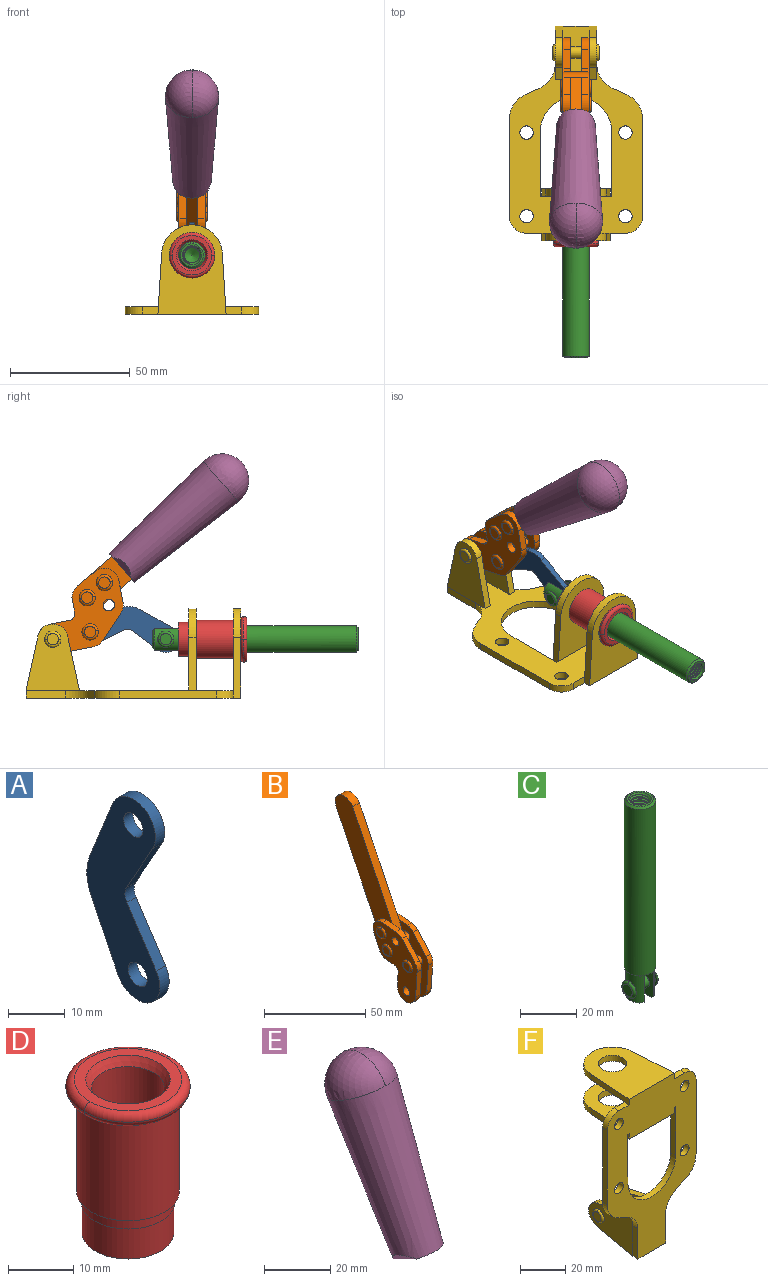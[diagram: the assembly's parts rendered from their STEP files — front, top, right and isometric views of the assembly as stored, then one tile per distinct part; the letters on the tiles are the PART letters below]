
ASSEMBLY  parts=6 mates=6
PART A: 12 faces, bbox 2.3x18.2x42.8 mm
  f0: cylinder r=2.4mm len=4.8mm, axis (1,0,0), area 34.9mm2, adj f4,f11
  f1: cylinder r=10.41mm len=8.47mm, axis (1,0,0), area 20.2mm2, adj f4,f9,f10,f11
  f2: cylinder r=3.05mm len=3.16mm, axis (1,0,0), area 7.7mm2, adj f4,f6,f7,f11
  f3: cylinder r=2.4mm len=4.8mm, axis (1,0,0), area 34.9mm2, adj f4,f11
  f4: plane 42.81x18.23mm, normal (-1,0,0), area 414.1mm2, adj f0,f1,f2,f3,f5,f6,f7,f8
  f5: cylinder r=5.54mm len=10.67mm, axis (1,0,0), area 41.8mm2, adj f4,f6,f10,f11
  f6: plane 11.66x6.53mm, normal (0,-0.87,-0.49), area 30.9mm2, adj f2,f4,f5,f11
  f7: plane 11.17x7.33mm, normal (0,-0.84,0.55), area 30.9mm2, adj f2,f4,f8,f11
  f8: cylinder r=5.54mm len=10.51mm, axis (1,0,0), area 41.8mm2, adj f4,f7,f9,f11
  f9: plane 13.67x6.67mm, normal (0,0.9,-0.44), area 35.1mm2, adj f1,f4,f8,f11
  f10: plane 14.1x5.7mm, normal (0,0.93,0.37), area 35.1mm2, adj f1,f4,f5,f11
  f11: plane 42.81x18.23mm, normal (1,0,0), area 414.1mm2, adj f0,f1,f2,f3,f5,f6,f7,f8
PART B: 59 faces, bbox 12.9x60.2x99.6 mm
  f0: torus R=2.39mm, axis (-1,0,0), area 14.9mm2, adj f20,f43,f51
  f1: torus R=2.39mm, axis (-1,0,0), area 14.9mm2, adj f19,f42,f51
  f2: torus R=2.39mm, axis (-1,0,0), area 14.9mm2, adj f18,f35,f51
  f3: torus R=2.39mm, axis (-1,0,0), area 14.9mm2, adj f14,f17,f23
  f4: torus R=2.39mm, axis (-1,0,0), area 14.9mm2, adj f13,f16,f23
  f5: torus R=2.39mm, axis (-1,0,0), area 14.9mm2, adj f12,f15,f23
  f6: cylinder r=2.39mm len=4.78mm, axis (1,0,0), area 46.5mm2, adj f48,f50,f51
  f7: cylinder r=2.39mm len=4.78mm, axis (1,0,0), area 46.5mm2, adj f50,f51
  f8: cylinder r=6.35mm len=12.68mm, axis (1,0,0), area 61.8mm2, adj f38,f39,f50,f51
  f9: cylinder r=2.39mm len=4.78mm, axis (-1,0,0), area 70.5mm2, adj f46,f50
  f10: cylinder r=2.39mm len=4.78mm, axis (-1,0,0), area 46.5mm2, adj f23,f45,f46
  f11: cylinder r=2.39mm len=4.78mm, axis (-1,0,0), area 46.5mm2, adj f23,f46
  f12: plane 4.78x4.78mm, normal (1,0,0), area 17.9mm2, adj f5,f15
  f13: plane 4.78x4.78mm, normal (1,0,0), area 17.9mm2, adj f4,f16
  f14: plane 4.78x4.78mm, normal (1,0,0), area 17.9mm2, adj f3,f17
  f15: torus R=2.39mm, axis (-1,0,0), area 14.9mm2, adj f5,f12,f23
  f16: torus R=2.39mm, axis (-1,0,0), area 14.9mm2, adj f4,f13,f23
  f17: torus R=2.39mm, axis (-1,0,0), area 14.9mm2, adj f3,f14,f23
  f18: plane 4.78x4.78mm, normal (-1,0,0), area 17.9mm2, adj f2,f35
  f19: plane 4.78x4.78mm, normal (-1,0,0), area 17.9mm2, adj f1,f42
  f20: plane 4.78x4.78mm, normal (-1,0,0), area 17.9mm2, adj f0,f43
  f21: plane 2.26x0.2mm, normal (1,0,0), area 0.2mm2, adj f31,f44
  f22: plane 2.26x0.2mm, normal (-1,0,0), area 0.2mm2, adj f41,f44
  f23: plane 39.37x30.77mm, normal (1,0,0), area 565.5mm2, adj f3,f4,f5,f10,f11,f15,f16,f17
  f24: cylinder r=6.1mm len=4.15mm, axis (-1,0,0), area 14.7mm2, adj f23,f25,f32,f46
  f25: plane 10.25x9.01mm, normal (0,-0.75,0.66), area 42.3mm2, adj f23,f24,f26,f46
  f26: cylinder r=6.35mm len=4.64mm, axis (-1,0,0), area 15.6mm2, adj f23,f25,f27,f46
  f27: plane 15.84x3.1mm, normal (0,-1,-0.07), area 49.2mm2, adj f23,f26,f28,f46
  f28: cylinder r=6.35mm len=12.68mm, axis (-1,0,0), area 61.8mm2, adj f23,f27,f29,f46
  f29: plane 8.11x3.1mm, normal (0,1,0.07), area 25.2mm2, adj f23,f28,f30,f46
  f30: cylinder r=3.05mm len=3.25mm, axis (-1,0,0), area 14.8mm2, adj f23,f29,f31,f46
  f31: plane 5.99x3.1mm, normal (0,0.07,-1), area 18.6mm2, adj f21,f23,f30,f44,f46
  f32: plane 9.5x3.1mm, normal (0,-0.07,1), area 29.5mm2, adj f23,f24,f33,f46,f47
  f33: cylinder r=6.1mm len=8.63mm, axis (-1,0,0), area 39.1mm2, adj f23,f32,f34,f47
  f34: plane 8.65x3.96mm, normal (0,0.91,-0.42), area 29.5mm2, adj f23,f33,f44,f47
  f35: torus R=2.39mm, axis (-1,0,0), area 14.9mm2, adj f2,f18,f51
  f36: plane 10.25x9.01mm, normal (0,-0.75,0.66), area 42.3mm2, adj f37,f49,f50,f51
  f37: cylinder r=6.35mm len=4.64mm, axis (1,0,0), area 15.6mm2, adj f36,f38,f50,f51
  f38: plane 15.84x3.1mm, normal (0,-1,-0.07), area 49.2mm2, adj f8,f37,f50,f51
  f39: plane 8.11x3.1mm, normal (0,1,0.07), area 25.2mm2, adj f8,f40,f50,f51
  f40: cylinder r=3.05mm len=3.25mm, axis (1,0,0), area 14.8mm2, adj f39,f41,f50,f51
  f41: plane 5.99x3.1mm, normal (0,0.07,-1), area 18.6mm2, adj f22,f40,f44,f50,f51
  f42: torus R=2.39mm, axis (-1,0,0), area 14.9mm2, adj f1,f19,f51
  f43: torus R=2.39mm, axis (-1,0,0), area 14.9mm2, adj f0,f20,f51
  f44: cylinder r=6.35mm len=12.12mm, axis (-1,0,0), area 128.9mm2, adj f21,f22,f23,f31,f34,f41,f46,f47
  f45: plane 2.65x1.35mm, normal (1,0,0), area 1mm2, adj f10,f55
  f46: plane 39.08x20.42mm, normal (-1,0,0), area 412.5mm2, adj f9,f10,f11,f24,f25,f26,f27,f28
  f47: plane 77.62x39.82mm, normal (1,0,0), area 850mm2, adj f32,f33,f34,f44,f53,f54,f55
  f48: plane 2.65x1.35mm, normal (-1,0,0), area 1mm2, adj f6,f55
  f49: cylinder r=6.1mm len=4.15mm, axis (1,0,0), area 14.7mm2, adj f36,f50,f51,f56
  f50: plane 39.08x20.42mm, normal (1,0,0), area 412.5mm2, adj f6,f7,f8,f9,f36,f37,f38,f39
  f51: plane 39.37x30.77mm, normal (-1,0,0), area 565.5mm2, adj f0,f1,f2,f6,f7,f8,f35,f36
  f52: plane 8.65x3.96mm, normal (0,0.91,-0.42), area 29.5mm2, adj f44,f51,f57,f58
  f53: plane 68.49x33.4mm, normal (0,0.9,-0.44), area 358.1mm2, adj f44,f47,f54,f58
  f54: cylinder r=6.35mm len=12.06mm, axis (1,0,0), area 93.7mm2, adj f47,f53,f55,f58
  f55: plane 68.49x33.4mm, normal (0,-0.9,0.44), area 358.1mm2, adj f44,f45,f46,f47,f48,f50,f54,f58
  f56: plane 9.5x3.1mm, normal (0,-0.07,1), area 29.5mm2, adj f49,f50,f51,f57,f58
  f57: cylinder r=6.1mm len=8.63mm, axis (1,0,0), area 39.1mm2, adj f51,f52,f56,f58
  f58: plane 77.62x39.82mm, normal (-1,0,0), area 850mm2, adj f44,f52,f53,f54,f55,f56,f57
PART C: 48 faces, bbox 12.6x11.1x86.1 mm
  f0: torus R=2.41mm, axis (-1,0,0), area 15mm2, adj f30,f32,f34
  f1: torus R=2.41mm, axis (-1,0,0), area 15mm2, adj f29,f31,f33
  f2: cylinder r=5.54mm len=72.39mm, axis (0,0,1), area 2518.5mm2, adj f3,f4,f42,f43
  f3: cone r=5.54mm half-angle=45deg, axis (0,0,1), area 7.6mm2, adj f2,f5,f41
  f4: cone r=5.54mm half-angle=45deg, axis (0,0,-1), area 34.9mm2, adj f2,f39
  f5: cylinder r=5.08mm len=11.48mm, axis (0,0,1), area 108.3mm2, adj f3,f7,f8,f41
  f6: cylinder r=2.41mm len=4.83mm, axis (-1,0,0), area 71.2mm2, adj f40,f41
  f7: cylinder r=2.41mm len=4.83mm, axis (-1,0,0), area 7.6mm2, adj f5,f34
  f8: cone r=5.08mm half-angle=45deg, axis (0,0,1), area 10.6mm2, adj f5,f37,f41
  f9: cone r=3.98mm half-angle=45deg, axis (0,0,1), area 17.6mm2, adj f27,f39,f45,f46,f47
  f10: cylinder r=2.41mm len=4.83mm, axis (-1,0,0), area 7.6mm2, adj f33,f38
  f11: cylinder r=3.2mm len=6.4mm, axis (0,0,1), area 78.4mm2, adj f12,f28,f44,f45,f47
  f12: cylinder r=3.2mm len=6.4mm, axis (0,0,1), area 10.5mm2, adj f11,f13,f45,f47
  f13: cylinder r=3.2mm len=6.4mm, axis (0,0,1), area 10.5mm2, adj f12,f14,f45,f47
  f14: cylinder r=3.2mm len=6.4mm, axis (0,0,1), area 10.5mm2, adj f13,f15,f45,f47
  f15: cylinder r=3.2mm len=6.4mm, axis (0,0,1), area 10.5mm2, adj f14,f16,f45,f47
  f16: cylinder r=3.2mm len=6.4mm, axis (0,0,1), area 10.5mm2, adj f15,f17,f45,f47
  f17: cylinder r=3.2mm len=6.4mm, axis (0,0,1), area 10.5mm2, adj f16,f18,f45,f47
  f18: cylinder r=3.2mm len=6.4mm, axis (0,0,1), area 10.5mm2, adj f17,f19,f45,f47
  f19: cylinder r=3.2mm len=6.4mm, axis (0,0,1), area 10.5mm2, adj f18,f20,f45,f47
  f20: cylinder r=3.2mm len=6.4mm, axis (0,0,1), area 10.5mm2, adj f19,f21,f45,f47
  f21: cylinder r=3.2mm len=6.4mm, axis (0,0,1), area 10.5mm2, adj f20,f22,f45,f47
  f22: cylinder r=3.2mm len=6.4mm, axis (0,0,1), area 10.5mm2, adj f21,f23,f45,f47
  f23: cylinder r=3.2mm len=6.4mm, axis (0,0,1), area 10.5mm2, adj f22,f24,f45,f47
  f24: cylinder r=3.2mm len=6.4mm, axis (0,0,1), area 10.5mm2, adj f23,f25,f45,f47
  f25: cylinder r=3.2mm len=6.4mm, axis (0,0,1), area 10.5mm2, adj f24,f26,f45,f47
  f26: cylinder r=3.2mm len=6.4mm, axis (0,0,1), area 10.5mm2, adj f25,f27,f45,f47
  f27: cylinder r=3.2mm len=6.4mm, axis (0,0,1), area 7.4mm2, adj f9,f26,f45,f47
  f28: cone r=3.2mm half-angle=60deg, axis (0,0,1), area 37.2mm2, adj f11
  f29: plane 4.83x4.83mm, normal (-1,0,0), area 18.3mm2, adj f1,f31
  f30: plane 4.83x4.83mm, normal (1,0,0), area 18.3mm2, adj f0,f32
  f31: torus R=2.41mm, axis (-1,0,0), area 15mm2, adj f1,f29,f33
  f32: torus R=2.41mm, axis (-1,0,0), area 15mm2, adj f0,f30,f34
  f33: plane 6.83x6.83mm, normal (1,0,0), area 18.3mm2, adj f1,f10,f31
  f34: plane 6.83x6.83mm, normal (-1,0,0), area 18.3mm2, adj f0,f7,f32
  f35: cone r=5.08mm half-angle=45deg, axis (0,0,1), area 10.6mm2, adj f36,f38,f40
  f36: plane 7.25x1.97mm, normal (0,0,-1), area 10mm2, adj f35,f40
  f37: plane 7.25x1.97mm, normal (0,0,-1), area 10mm2, adj f8,f41
  f38: cylinder r=5.08mm len=11.48mm, axis (0,0,1), area 108.3mm2, adj f10,f35,f40,f42
  f39: plane 9.55x9.55mm, normal (0,0,1), area 22mm2, adj f4,f9
  f40: plane 12.76x10.09mm, normal (1,0,0), area 95.7mm2, adj f6,f35,f36,f38,f42,f43
  f41: plane 12.76x10.09mm, normal (-1,0,0), area 95.7mm2, adj f3,f5,f6,f8,f37,f43
  f42: cone r=5.54mm half-angle=45deg, axis (0,0,1), area 7.6mm2, adj f2,f38,f40
  f43: plane 11.07x4.7mm, normal (0,0,-1), area 50.4mm2, adj f2,f40,f41
  f44: plane 0.89x0.62mm, normal (-1,0,0), area 0.3mm2, adj f11,f45,f46,f47
  f45: bspline ~24.8x7.63mm, area 266.6mm2, adj f9,f11,f12,f13,f14,f15,f16,f17
  f46: bspline ~24.87x7.63mm, area 73.6mm2, adj f9,f44,f45,f47
  f47: bspline ~24.98x7.63mm, area 272.5mm2, adj f9,f11,f12,f13,f14,f15,f16,f17
PART D: 15 faces, bbox 20.6x20.6x28.7 mm
  f0: torus R=8.26mm, axis (0,0,1), area 56.8mm2, adj f1,f10,f12
  f1: torus R=8.26mm, axis (0,0,1), area 56.8mm2, adj f0,f6,f13
  f2: cylinder r=5.59mm len=25.91mm, axis (0,0,1), area 909.6mm2, adj f3,f4
  f3: cone r=6.86mm half-angle=45deg, axis (0,0,-1), area 70.2mm2, adj f2,f14
  f4: cone r=6.47mm half-angle=30deg, axis (0,0,1), area 66.7mm2, adj f2,f13
  f5: cylinder r=7.04mm len=14.07mm, axis (0,0,1), area 252.6mm2, adj f11,f14
  f6: torus R=8.26mm, axis (0,0,1), area 56.8mm2, adj f1,f12,f13
  f7: cylinder r=7.16mm len=14.33mm, axis (0,0,1), area 91.5mm2, adj f9,f11
  f8: cylinder r=7.86mm len=18.42mm, axis (0,0,1), area 909.6mm2, adj f9,f10
  f9: plane 15.72x15.72mm, normal (0,0,-1), area 33mm2, adj f7,f8
  f10: plane 16.51x16.51mm, normal (0,0,-1), area 19.9mm2, adj f0,f8,f12
  f11: plane 14.33x14.33mm, normal (0,0,-1), area 5.7mm2, adj f5,f7
  f12: torus R=8.26mm, axis (0,0,1), area 56.8mm2, adj f0,f6,f10
  f13: plane 16.51x16.51mm, normal (0,0,1), area 82.7mm2, adj f1,f4,f6
  f14: plane 14.07x14.07mm, normal (0,0,-1), area 7.8mm2, adj f3,f5
PART E: 11 faces, bbox 22.3x42.6x64.5 mm
  f0: sphere r=11.13mm, area 411.4mm2, adj f1,f8
  f1: cone r=11.11mm half-angle=3.3deg, axis (0,0.44,0.9), area 3251.8mm2, adj f0,f7,f8,f9,f10
  f2: cylinder r=6.16mm len=11.7mm, axis (1,0,0), area 89.5mm2, adj f3,f4,f5,f6
  f3: plane 60.23x36.75mm, normal (-1,0,0), area 763.6mm2, adj f2,f4,f6,f10
  f4: plane 51.37x25.05mm, normal (0,0.9,-0.44), area 264.2mm2, adj f2,f3,f5,f10
  f5: plane 60.23x36.75mm, normal (1,0,0), area 763.6mm2, adj f2,f4,f6,f10
  f6: plane 51.37x25.05mm, normal (0,-0.9,0.44), area 264.2mm2, adj f2,f3,f5,f10
  f7: plane 9.95x5.95mm, normal (0.71,-0.31,-0.64), area 25.8mm2, adj f1,f10
  f8: sphere r=11.13mm, area 411.4mm2, adj f0,f1
  f9: plane 9.95x5.95mm, normal (-0.71,-0.31,-0.64), area 25.8mm2, adj f1,f10
  f10: plane 14.27x11.38mm, normal (0,-0.44,-0.9), area 106.7mm2, adj f1,f3,f4,f5,f6,f7,f9
PART F: 55 faces, bbox 55.7x37.4x89.8 mm
  f0: torus R=2.41mm, axis (-1,0,0), area 15mm2, adj f11,f15,f25
  f1: torus R=2.41mm, axis (-1,0,0), area 15mm2, adj f10,f12,f22
  f2: cylinder r=2.78mm len=5.56mm, axis (0,-1,0), area 54.2mm2, adj f30,f54
  f3: cylinder r=14.99mm len=29.97mm, axis (0,-1,0), area 145.9mm2, adj f30,f49,f53,f54
  f4: cylinder r=2.78mm len=5.56mm, axis (0,-1,0), area 54.2mm2, adj f30,f54
  f5: cylinder r=2.78mm len=5.56mm, axis (0,-1,0), area 54.2mm2, adj f30,f54
  f6: cylinder r=2.78mm len=5.56mm, axis (0,-1,0), area 54.2mm2, adj f30,f54
  f7: cylinder r=6.35mm len=12.7mm, axis (0,0,1), area 123.6mm2, adj f27,f51
  f8: cylinder r=6.35mm len=12.7mm, axis (0,0,-1), area 124.7mm2, adj f21,f35
  f9: cylinder r=2.41mm len=11.18mm, axis (-1,0,0), area 169.4mm2, adj f16,f19
  f10: plane 4.83x4.83mm, normal (1,0,0), area 18.3mm2, adj f1,f12
  f11: plane 4.83x4.83mm, normal (-1,0,0), area 18.3mm2, adj f0,f15
  f12: torus R=2.41mm, axis (-1,0,0), area 15mm2, adj f1,f10,f22
  f13: cylinder r=6.35mm len=12.41mm, axis (1,0,0), area 53.4mm2, adj f18,f19,f22,f23
  f14: cylinder r=6.35mm len=12.41mm, axis (-1,0,0), area 53.4mm2, adj f16,f17,f24,f25
  f15: torus R=2.41mm, axis (-1,0,0), area 15mm2, adj f0,f11,f25
  f16: plane 27.86x22.35mm, normal (1,0,0), area 425.4mm2, adj f9,f14,f17,f24,f30
  f17: plane 22.86x4.97mm, normal (0,0.21,0.98), area 72.5mm2, adj f14,f16,f25,f30
  f18: plane 22.86x4.97mm, normal (0,0.21,0.98), area 72.5mm2, adj f13,f19,f22,f30
  f19: plane 27.86x22.35mm, normal (-1,0,0), area 425.4mm2, adj f9,f13,f18,f23,f30
  f20: cylinder r=12.7mm len=25.35mm, axis (0,0,-1), area 119.8mm2, adj f21,f34,f35,f36
  f21: plane 34.21x28.07mm, normal (0,0,-1), area 702.4mm2, adj f8,f20,f30,f34,f36
  f22: plane 27.96x22.45mm, normal (1,0,0), area 407.2mm2, adj f1,f12,f13,f18,f23,f30,f42,f43
  f23: plane 22.86x4.97mm, normal (0,0.21,-0.98), area 72.5mm2, adj f13,f19,f22,f44
  f24: plane 22.86x4.97mm, normal (0,0.21,-0.98), area 72.5mm2, adj f14,f16,f25,f44
  f25: plane 27.86x22.35mm, normal (-1,0,0), area 407.1mm2, adj f0,f14,f15,f17,f24,f30,f45,f46
  f26: plane 3.1x0.95mm, normal (0,0,-1), area 2.7mm2, adj f30,f49,f50,f54
  f27: plane 34.21x28.07mm, normal (0,0,1), area 702.4mm2, adj f7,f28,f30,f50,f52
  f28: cylinder r=12.7mm len=25.35mm, axis (0,0,1), area 118.8mm2, adj f27,f50,f51,f52
  f29: plane 3.1x0.95mm, normal (0,0,-1), area 2.7mm2, adj f30,f52,f53,f54
  f30: plane 86.54x55.63mm, normal (0,1,0), area 2362.9mm2, adj f2,f3,f4,f5,f6,f16,f17,f18
  f31: plane 40.56x3.1mm, normal (-1,0,0), area 125.7mm2, adj f30,f32,f48,f54
  f32: cylinder r=7.11mm len=7.11mm, axis (0,-1,0), area 34.6mm2, adj f30,f31,f33,f54
  f33: plane 6.67x3.1mm, normal (0,0,1), area 20.4mm2, adj f30,f32,f34,f54
  f34: plane 25.39x3.13mm, normal (-1,0.06,0), area 79.5mm2, adj f20,f21,f33,f35,f54
  f35: plane 37.31x28.45mm, normal (0,0,1), area 789.9mm2, adj f8,f20,f34,f36,f54
  f36: plane 25.39x3.13mm, normal (1,0.06,0), area 79.5mm2, adj f20,f21,f35,f37,f54
  f37: plane 6.67x3.1mm, normal (0,0,1), area 20.4mm2, adj f30,f36,f38,f54
  f38: cylinder r=7.11mm len=7.11mm, axis (0,-1,0), area 34.6mm2, adj f30,f37,f39,f54
  f39: plane 40.56x3.1mm, normal (1,0,0), area 125.7mm2, adj f30,f38,f40,f54
  f40: cylinder r=11.18mm len=10.16mm, axis (0,-1,0), area 39.5mm2, adj f30,f39,f41,f54
  f41: plane 6.09x3.1mm, normal (0.42,0,-0.91), area 20.8mm2, adj f30,f40,f42,f54
  f42: cylinder r=11.18mm len=9.41mm, axis (0,-1,0), area 37.2mm2, adj f22,f30,f41,f43,f54
  f43: plane 16.5x3.1mm, normal (1,0,0), area 51.1mm2, adj f22,f42,f44,f54
  f44: plane 17.37x3.1mm, normal (0,0,-1), area 53.8mm2, adj f23,f24,f30,f43,f45,f54
  f45: plane 16.5x3.1mm, normal (-1,0,0), area 51.1mm2, adj f25,f44,f46,f54
  f46: cylinder r=11.18mm len=9.41mm, axis (0,-1,0), area 37.2mm2, adj f25,f30,f45,f47,f54
  f47: plane 6.09x3.1mm, normal (-0.42,0,-0.91), area 20.8mm2, adj f30,f46,f48,f54
  f48: cylinder r=11.18mm len=10.16mm, axis (0,-1,0), area 39.5mm2, adj f30,f31,f47,f54
  f49: plane 26.54x3.1mm, normal (-1,0,0), area 82.3mm2, adj f3,f26,f30,f54
  f50: plane 25.39x3.1mm, normal (1,0.06,0), area 78.8mm2, adj f26,f27,f28,f51,f54
  f51: plane 37.31x28.45mm, normal (0,0,-1), area 789.9mm2, adj f7,f28,f50,f52,f54
  f52: plane 25.39x3.1mm, normal (-1,0.06,0), area 78.8mm2, adj f27,f28,f29,f51,f54
  f53: plane 26.54x3.1mm, normal (1,0,0), area 82.3mm2, adj f3,f29,f30,f54
  f54: plane 89.66x55.63mm, normal (0,-1,0), area 2678.5mm2, adj f2,f3,f4,f5,f6,f26,f29,f31
PLACE A rot(axis=(1,0,0),97.5deg) t=(0,12.59,2.22)mm
PLACE B rot(axis=(1,0,0),75deg) t=(0,3.86,9.14)mm
PLACE C rot(axis=(1,0,0),90deg) t=(0,9.52,0)mm
PLACE D rot(axis=(1,0,0),90deg) t=(0,9.14,0)mm
PLACE E rot(axis=(1,0,0),75deg) t=(0,3.86,9.14)mm
PLACE F rot(axis=(1,0,0),90deg) t=(0,9.14,0)mm fixed
MATE slider C.f2 <-> F.f7  axis (0,-1,0) through (0,-49.26,24.61)mm
MATE fastened D.f2 <-> F.f7  axis (0,-1,0) through (0,-37.25,24.61)mm
MATE revolute A.f3 <-> B.f4  axis (1,0,0) through (0,25.65,27.64)mm
MATE fastened E.f2 <-> B.f54  axis (1,0,0) through (0,-30.66,91.94)mm
MATE revolute B.f7 <-> F.f0  axis (1,0,0) through (0,41.23,24.61)mm
MATE revolute A.f5 <-> C.f6  axis (1,0,0) through (0,-5.96,24.61)mm
